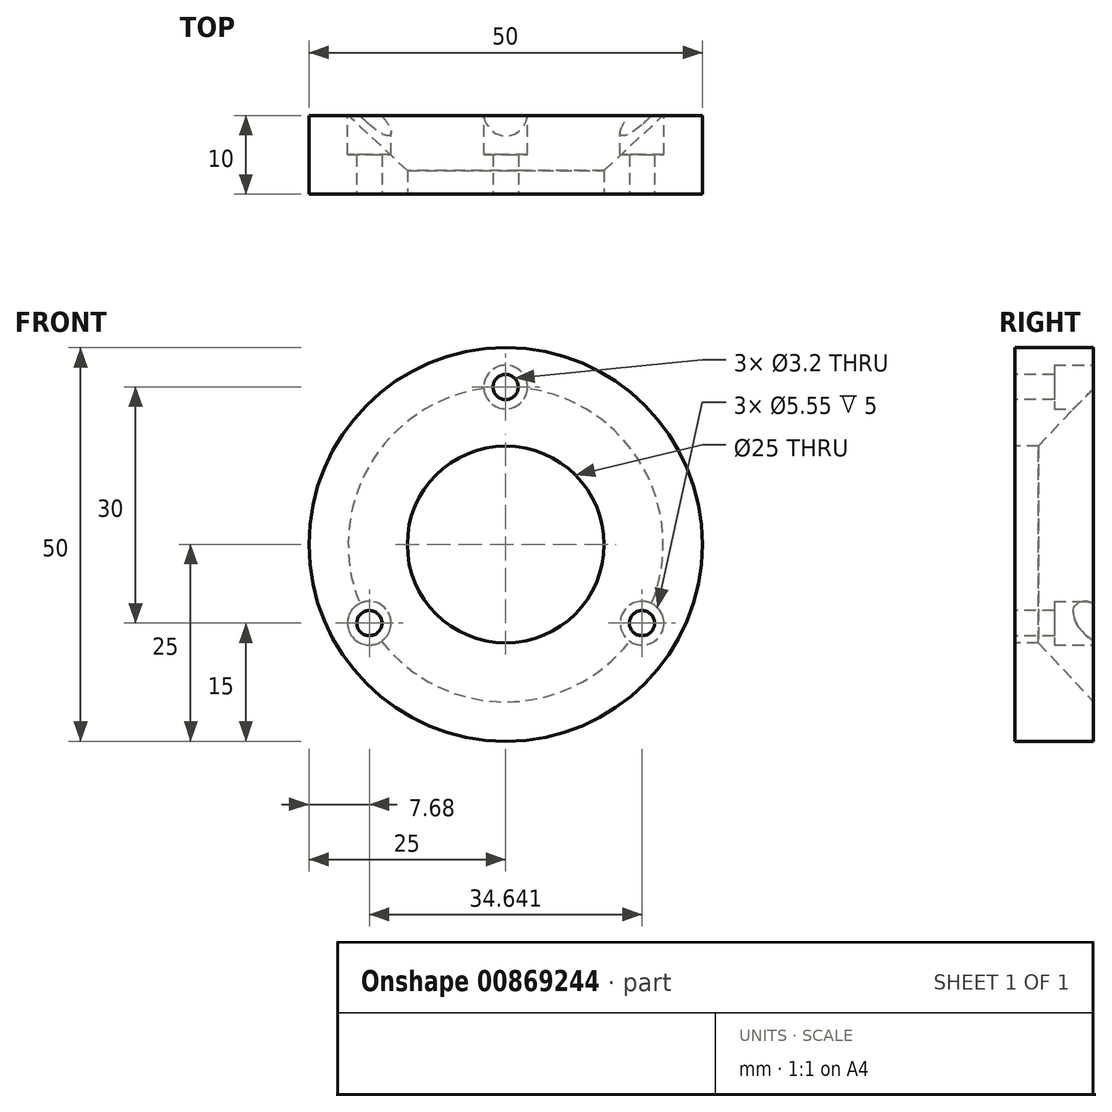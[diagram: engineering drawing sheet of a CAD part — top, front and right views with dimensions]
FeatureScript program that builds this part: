
annotation { "Feature Type Name" : "Feature", "Feature Type Description" : "" }
export const myFeature = defineFeature(function(context is Context, id is Id, definition is map)
    precondition{}
    {
        {
            var Q0;
            Q0=qCreatedBy(makeId("Top.planeOp"),FACE);
            var sketch = newSketch(context, id + "F0", { "sketchPlane" : qUnion([Q0])});
            skLineSegment(sketch, "E0", {"start": v(12.5, 0) * mm, "end": v(12.5, 3) * mm});
            skLineSegment(sketch, "E1", {"start": v(12.5, 3) * mm, "end": v(20, 10) * mm});
            skLineSegment(sketch, "E2", {"start": v(20, 10) * mm, "end": v(25, 10) * mm});
            skLineSegment(sketch, "E3", {"start": v(25, 10) * mm, "end": v(25, 0) * mm});
            skLineSegment(sketch, "E4", {"start": v(25, 0) * mm, "end": v(12.5, 0) * mm});
            skSolve(sketch);
        }
        {
            var Q0;
            Q0=qCreatedBy(makeId("Top.planeOp"),FACE);
            var sketch = newSketch(context, id + "F1", { "sketchPlane" : qUnion([Q0])});
            skLineSegment(sketch, "E5", {"start": v(0, 0) * mm, "end": v(0, 58.2) * mm});
            skSolve(sketch);
        }
        {
            var Q0;
            Q0 = qSketchRegion(id + "F0", true);
            var Q1;
            Q1=sQuery(id+"F1.wireOp",EDGE,"E5");
            revolve(context, id + "F2", {"surfaceOperationType" : NewSurfaceOperationType.NEW, "entities" : qUnion([Q0]), "axis" : qUnion([Q1]), "revolveType" : RevolveType.FULL});
        }
        {
            var Q0;
            Q0=makeQuery(id+"F2.opRevolve","SWEPT_FACE",FACE,{"disambiguationData":[OSD([sQuery(id+"F0.wireOp",EDGE,"E4")])]});
            var sketch = newSketch(context, id + "F3", { "sketchPlane" : qUnion([Q0])});
            skCircle(sketch, "E6", {"center": v(0, 20) * mm, "radius": 1.6 * mm});
            skCircle(sketch, "E7.1.0", {"center": v(-17.32, -10) * mm, "radius": 1.6 * mm});
            skCircle(sketch, "E7.2.0", {"center": v(17.32, -10) * mm, "radius": 1.6 * mm});
            skPoint(sketch, "E7.center", {"position": v(0, 0) * mm});
            skSolve(sketch);
        }
        {
            var Q0;
            Q0 = qSketchRegion(id + "F3", true);
            extrude(context, id + "F4", {"entities" : qUnion([Q0]), "operationType" : NewBodyOperationType.REMOVE, "oppositeDirection" : true, "depth" : 25 * mm, "offsetDistance" : 25 * mm});
        }
        {
            var Q0;
            Q0=makeQuery(id+"F2.opRevolve","SWEPT_FACE",FACE,{"disambiguationData":[OSD([sQuery(id+"F0.wireOp",EDGE,"E2")])]});
            var sketch = newSketch(context, id + "F5", { "sketchPlane" : qUnion([Q0])});
            skCircle(sketch, "E8", {"center": v(0, 20) * mm, "radius": 2.77 * mm});
            skCircle(sketch, "E9.1.0", {"center": v(-17.32, -10) * mm, "radius": 2.77 * mm});
            skCircle(sketch, "E9.2.0", {"center": v(17.32, -10) * mm, "radius": 2.77 * mm});
            skPoint(sketch, "E9.center", {"position": v(0, 0) * mm});
            skSolve(sketch);
        }
        {
            var Q0;
            Q0 = qSketchRegion(id + "F5", true);
            extrude(context, id + "F6", {"entities" : qUnion([Q0]), "operationType" : NewBodyOperationType.REMOVE, "oppositeDirection" : true, "depth" : 5 * mm, "offsetDistance" : 25 * mm});
        }
    });
